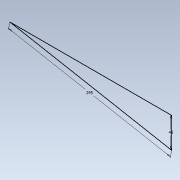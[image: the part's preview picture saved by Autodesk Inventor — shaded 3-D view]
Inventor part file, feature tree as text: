
AUTODESK INVENTOR PART (.ipt)
format: ipt  version: 2021 (Build 250183000, 183)  size: 68,608 bytes
history: native  units: mm
features: sketch x1
ambient origin geometry x8: Origin, YZ Plane, XZ Plane, XY Plane, X Axis, Y Axis, Z Axis, Center Point
feature tree (1):
  sketch  "Sketch1"  dims[d0=45.0mm d1=245.0mm]
